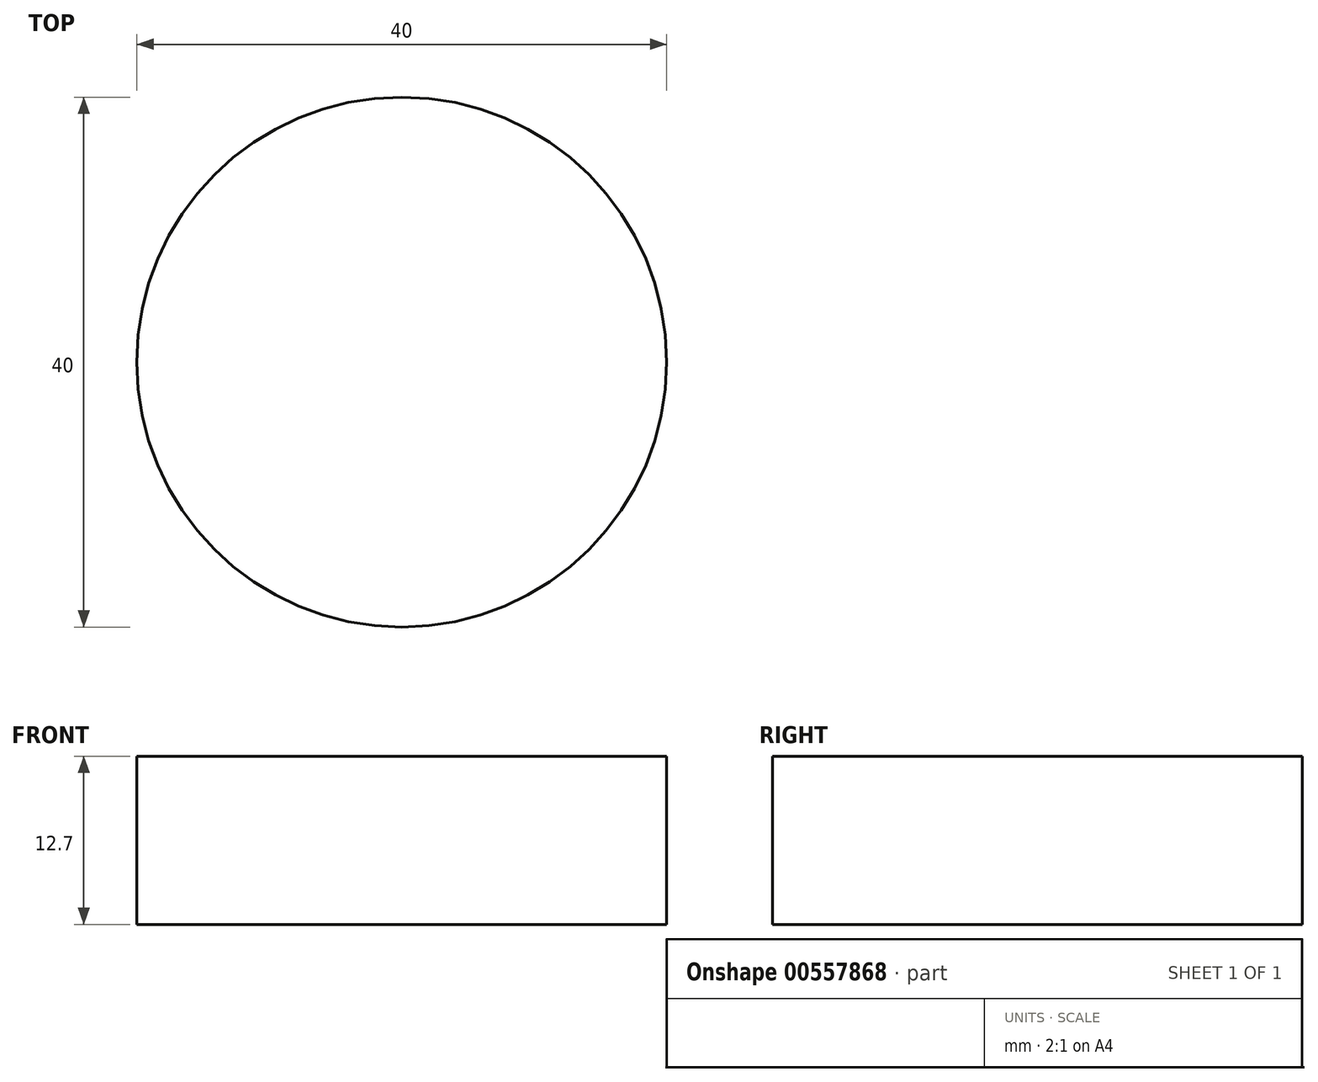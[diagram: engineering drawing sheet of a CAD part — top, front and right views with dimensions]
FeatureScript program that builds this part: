
annotation { "Feature Type Name" : "Feature", "Feature Type Description" : "" }
export const myFeature = defineFeature(function(context is Context, id is Id, definition is map)
    precondition{}
    {
        {
            var Q0;
            Q0=qCreatedBy(makeId("Top.planeOp"),FACE);
            var sketch = newSketch(context, id + "F0", { "sketchPlane" : qUnion([Q0])});
            skCircle(sketch, "E0", {"center": v(0, 0) * mm, "radius": 20 * mm});
            skSolve(sketch);
        }
        {
            var Q0;
            Q0=qSketchRegion(id+"F0",true);
            extrude(context, id + "F1", {"entities" : qUnion([Q0]), "depth" : 12.7 * mm, "offsetDistance" : 25.4 * mm});
        }
    });
